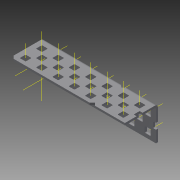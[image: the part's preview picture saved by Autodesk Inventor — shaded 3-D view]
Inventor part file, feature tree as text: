
AUTODESK INVENTOR PART (.ipt)
format: ipt  version: 2015 SP1 (Build 190203100, 203)  size: 1,972,736 bytes
history: native  units: in
note: dims shown in document units (in); Inventor stores cm internally (conversion verified against a paired STEP export)
features: other x47, pattern_linear x4, sheet_metal_op x1, extrude x1, imported_body x1, sketch x1
ambient origin geometry x8: Origin, YZ Plane, XZ Plane, XY Plane, X Axis, Y Axis, Z Axis, Center Point
bodies: Body1 (feature_tree)
feature tree (55):
  sheet_metal_op  "Fold1"
  other  "L-Channel"
  extrude  "length cut"  Depth=0.5in
  other  "top out axis"
  other  "top inner axis"
  other  "back out axis"
  other  "back inner axis"
  pattern_linear  "top outer axes"  Count1=2 Spacing1=0.5in
  pattern_linear  "top inner axes"  Spacing1=0.5in  [1 undecoded]
  pattern_linear  "back outer axes"  Count1=2 Spacing1=0.5in
  pattern_linear  "back inner axes"  Spacing1=0.5in  [1 undecoded]
  other  "right plane"
  imported_body  "Base1"
  sketch  "Sketch1"  dims[d1=0.0in d4=0.5in d5=0.7874in d7=0.5in d10=0.5in d13=0.5in d14=0.7874in d16=0.5in d19=0.5in d20=-3.5in d21=0.0in d22=0.0in d23=0.0in d24=0.0in d25=0.0in d26=0.0in]
  other  "Work Point1"
  other  "Work Point2"
  other  "Work Point3"
  other  "Work Point4"
  other  "Work Axis5"
  other  "Work Axis6"
  other  "Work Axis7"
  other  "Work Axis8"
  other  "Work Axis11"
  other  "Work Axis12"
  other  "Work Axis13"
  other  "Work Axis14"
  other  "Work Axis15"
  other  "Work Axis18"
  other  "Work Axis19"
  other  "Work Axis20"
  other  "Work Axis23"
  other  "Work Axis24"
  other  "Work Axis25"
  other  "Work Axis26"
  other  "Work Axis29"
  other  "Work Axis30"
  other  "Work Axis31"
  other  "Work Axis32"
  other  "Work Axis33"
  other  "Work Axis36"
  other  "Work Axis37"
  other  "Work Axis38"
  other  "left plane"
  other  "Work Axis173"
  other  "Work Axis174"
  other  "Work Axis175"
  other  "Work Axis176"
  other  "Work Axis177"
  other  "Work Axis178"
  other  "Work Axis179"
  other  "Work Axis180"
  other  "Work Axis181"
  other  "Work Axis182"
  other  "Work Axis183"
  other  "Work Axis184"
note: 2 required parameter values undecoded (feature->parameter linkage not recoverable at this tier; creation-order binding heuristic only, values carry confidence <= 0.55)
